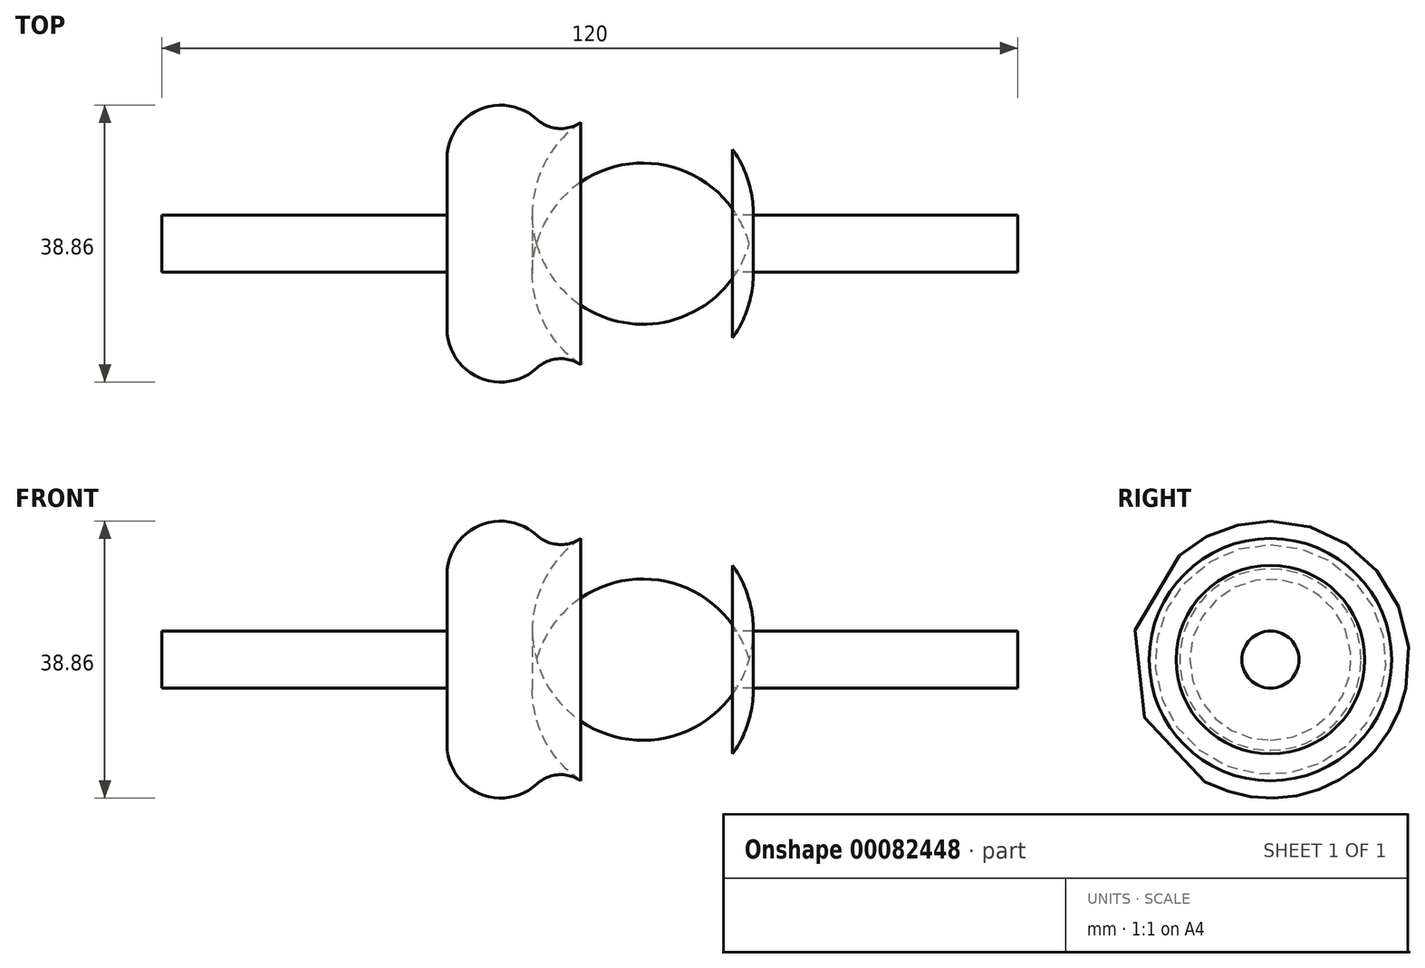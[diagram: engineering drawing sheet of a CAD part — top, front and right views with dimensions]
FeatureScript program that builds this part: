
annotation { "Feature Type Name" : "Feature", "Feature Type Description" : "" }
export const myFeature = defineFeature(function(context is Context, id is Id, definition is map)
    precondition{}
    {
        {
            var Q0;
            Q0=qCreatedBy(makeId("Front.planeOp"),FACE);
            var sketch = newSketch(context, id + "F0", { "sketchPlane" : qUnion([Q0])});
            skLineSegment(sketch, "E0.bottom", {"start": v(-120, 0) * mm, "end": v(0, 0) * mm});
            skLineSegment(sketch, "E0.top", {"start": v(-120, 4) * mm, "end": v(0, 4) * mm});
            skLineSegment(sketch, "E0.left", {"start": v(-120, 0) * mm, "end": v(-120, 4) * mm});
            skLineSegment(sketch, "E0.right", {"start": v(0, 0) * mm, "end": v(0, 4) * mm});
            skLineSegment(sketch, "E1.bottom", {"start": v(-80, 0) * mm, "end": v(-40, 0) * mm});
            skLineSegment(sketch, "E1.top", {"start": v(-80, 20) * mm, "end": v(-40, 20) * mm});
            skLineSegment(sketch, "E1.left", {"start": v(-80, 0) * mm, "end": v(-80, 20) * mm});
            skLineSegment(sketch, "E1.right", {"start": v(-40, 0) * mm, "end": v(-40, 20) * mm});
            skArc(sketch, "E2", {"start": v(-67.47, 17.46) * mm, "mid": v(-68.82, 18.44) * mm, "end": v(-70.35, 19.1) * mm});
            skArc(sketch, "E3", {"start": v(-40, 13.23) * mm, "mid": v(-43.93, 17.04) * mm, "end": v(-48.93, 19.24) * mm});
            skPoint(sketch, "E4.visualSharp", {"position": v(-65.15, 13.23) * mm});
            skArc(sketch, "E4.filletArc", {"start": v(-67.47, 17.46) * mm, "mid": v(-64.45, 16.15) * mm, "end": v(-61.28, 17) * mm});
            skArc(sketch, "E5", {"start": v(-75.04, 19) * mm, "mid": v(-78.43, 16.58) * mm, "end": v(-80, 12.72) * mm});
            skArc(sketch, "E6", {"start": v(-70.35, 19.1) * mm, "mid": v(-72.7, 19.43) * mm, "end": v(-75.04, 19) * mm});
            skArc(sketch, "E7", {"start": v(-55.74, 19.35) * mm, "mid": v(-58.62, 18.45) * mm, "end": v(-61.28, 17) * mm});
            skArc(sketch, "E8", {"start": v(-48.93, 19.24) * mm, "mid": v(-52.33, 19.67) * mm, "end": v(-55.74, 19.35) * mm});
            skSolve(sketch);
        }
        {
            var Q0;
            {var subQ0=sQuery(id+"F0.wireOp",EDGE,"E1.left");var subQ1=sQuery(id+"F0.wireOp",EDGE,"E0.top");var subQ2=makeQuery(id+"F0.imprint","INTERSECT",VERTEX,{"derivedFrom":[subQ1,subQ0]});Q0=makeQuery(id+"F0.imprint","IMPRINT",FACE,{"disambiguationData":[TD([[makeQuery(id+"F0.imprint","IMPRINT",EDGE,{"disambiguationData":[TD([[subQ2,-1.0]])],"derivedFrom":subQ1}),-1.0]])]});}
            var Q1;
            {var subQ0=sQuery(id+"F0.wireOp",EDGE,"E1.right");var subQ1=sQuery(id+"F0.wireOp",EDGE,"E0.top");var subQ2=makeQuery(id+"F0.imprint","INTERSECT",VERTEX,{"derivedFrom":[subQ1,subQ0]});Q1=makeQuery(id+"F0.imprint","IMPRINT",FACE,{"disambiguationData":[TD([[makeQuery(id+"F0.imprint","IMPRINT",EDGE,{"disambiguationData":[TD([[subQ2,1.0]])],"derivedFrom":subQ1}),-1.0]])]});}
            var Q2;
            {var subQ5=sQuery(id+"F0.wireOp",EDGE,"zeMAIKNO-UHNe-XGGX-103M-HygieYNwF2f8");Q2=makeQuery(id+"F0.imprint","IMPRINT",FACE,{"disambiguationData":[TD([[makeQuery(id+"F0.imprint","IMPRINT",EDGE,{"derivedFrom":subQ5}),1.0]])]});}
            var Q3;
            {var subQ4=sQuery(id+"F0.wireOp",EDGE,"E1.left");var subQ7=sQuery(id+"F0.wireOp",EDGE,"E0.top");var subQ8=makeQuery(id+"F0.imprint","INTERSECT",VERTEX,{"derivedFrom":[subQ7,subQ4]});Q3=makeQuery(id+"F0.imprint","IMPRINT",FACE,{"disambiguationData":[TD([[makeQuery(id+"F0.imprint","IMPRINT",EDGE,{"disambiguationData":[TD([[subQ8,-1.0]])],"derivedFrom":subQ7}),1.0]])]});}
            var Q4;
            {var subQ0=sQuery(id+"F0.wireOp",EDGE,"8W0RL3ST-54rh-zNx8-torv-IzC0xaJFQPJy");var subQ1=sQuery(id+"F0.wireOp",EDGE,"E1.top");var subQ2=makeQuery(id+"F0.imprint","INTERSECT",VERTEX,{"disambiguationData":[OD(0.0)],"derivedFrom":[subQ1,subQ0]});Q4=makeQuery(id+"F0.imprint","IMPRINT",FACE,{"disambiguationData":[TD([[makeQuery(id+"F0.imprint","IMPRINT",EDGE,{"disambiguationData":[TD([[subQ2,-1.0]])],"derivedFrom":subQ1}),1.0]])]});}
            var Q5;
            {var subQ0=sQuery(id+"F0.wireOp",EDGE,"0SkZrILY-crhI-tmVG-2EHV-gnY6IfGEYoPA");var subQ1=sQuery(id+"F0.wireOp",EDGE,"E1.top");var subQ2=makeQuery(id+"F0.imprint","INTERSECT",VERTEX,{"disambiguationData":[OD(0.0)],"derivedFrom":[subQ1,subQ0]});Q5=makeQuery(id+"F0.imprint","IMPRINT",FACE,{"disambiguationData":[TD([[makeQuery(id+"F0.imprint","IMPRINT",EDGE,{"disambiguationData":[TD([[subQ2,-1.0]])],"derivedFrom":subQ1}),1.0]])]});}
            var Q6;
            Q6=sQuery(id+"F0.wireOp",EDGE,"E1.bottom");
            revolve(context, id + "F1", {"entities" : qUnion([Q0, Q1, Q2, Q3, Q4, Q5]), "axis" : qUnion([Q6]), "revolveType" : RevolveType.FULL});
        }
        {
            var Q0;
            {var subQ0=sQuery(id+"F0.wireOp",EDGE,"E0.left");Q0=makeQuery(id+"F0.imprint","IMPRINT",FACE,{"disambiguationData":[TD([[makeQuery(id+"F0.imprint","IMPRINT",EDGE,{"derivedFrom":subQ0}),-1.0]])]});}
            var Q1;
            {var subQ0=sQuery(id+"F0.wireOp",EDGE,"E0.right");Q1=makeQuery(id+"F0.imprint","IMPRINT",FACE,{"disambiguationData":[TD([[makeQuery(id+"F0.imprint","IMPRINT",EDGE,{"derivedFrom":subQ0}),1.0]])]});}
            var Q2;
            Q2=sQuery(id+"F0.wireOp",EDGE,"E1.bottom");
            revolve(context, id + "F2", {"entities" : qUnion([Q0, Q1]), "axis" : qUnion([Q2]), "revolveType" : RevolveType.FULL});
        }
        {
            var Q0;
            Q0=sQuery(id+"F0.wireOp",EDGE,"E6");
            var Q1;
            Q1=sQuery(id+"F0.wireOp",EDGE,"E8");
            var Q2;
            Q2=sQuery(id+"F0.wireOp",EDGE,"E1.bottom");
            revolve(context, id + "F3", {"bodyType" : ToolBodyType.SURFACE, "surfaceEntities" : qUnion([Q0, Q1]), "axis" : qUnion([Q2]), "revolveType" : RevolveType.FULL});
        }
    });
